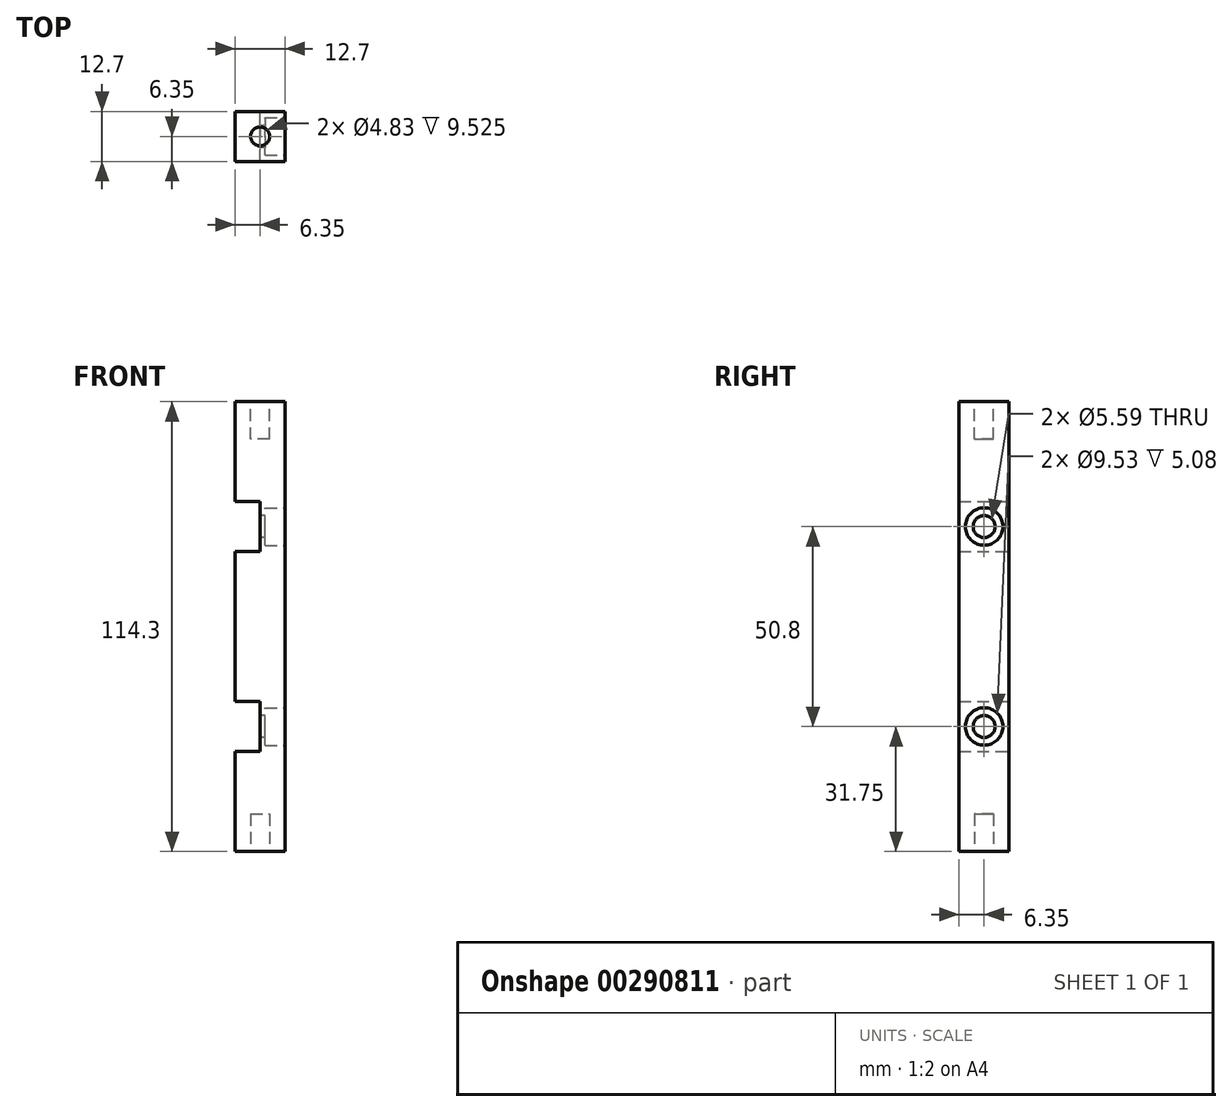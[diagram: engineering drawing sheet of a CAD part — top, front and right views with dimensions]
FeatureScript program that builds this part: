
annotation { "Feature Type Name" : "Feature", "Feature Type Description" : "" }
export const myFeature = defineFeature(function(context is Context, id is Id, definition is map)
    precondition{}
    {
        {
            var Q0;
            Q0=qCreatedBy(makeId("Right.planeOp"),FACE);
            var sketch = newSketch(context, id + "F0", { "sketchPlane" : qUnion([Q0])});
            skLineSegment(sketch, "E0.bottom", {"start": v(-12.7, 57.15) * mm, "end": v(0, 57.15) * mm});
            skLineSegment(sketch, "E0.top", {"start": v(-12.7, -57.15) * mm, "end": v(0, -57.15) * mm});
            skLineSegment(sketch, "E0.left", {"start": v(-12.7, 57.15) * mm, "end": v(-12.7, -57.15) * mm});
            skLineSegment(sketch, "E0.right", {"start": v(0, 57.15) * mm, "end": v(0, -57.15) * mm});
            skSolve(sketch);
        }
        {
            var Q0;
            Q0 = qSketchRegion(id + "F0", true);
            extrude(context, id + "F1", {"entities" : qUnion([Q0]), "depth" : 12.7 * mm});
        }
        {
            var Q0;
            Q0=makeQuery(id+"F1.opExtrude","SWEPT_FACE",FACE,{"disambiguationData":[OSD([sQuery(id+"F0.wireOp",EDGE,"E0.right")])]});
            var sketch = newSketch(context, id + "F2", { "sketchPlane" : qUnion([Q0])});
            skLineSegment(sketch, "E1.bottom", {"start": v(-6.35, 19.05) * mm, "end": v(0, 19.05) * mm});
            skLineSegment(sketch, "E1.top", {"start": v(-6.35, 31.75) * mm, "end": v(0, 31.75) * mm});
            skLineSegment(sketch, "E1.left", {"start": v(-6.35, 19.05) * mm, "end": v(-6.35, 31.75) * mm});
            skLineSegment(sketch, "E1.right", {"start": v(0, 19.05) * mm, "end": v(0, 31.75) * mm});
            skLineSegment(sketch, "E2.0.1.0", {"start": v(0, -31.75) * mm, "end": v(0, -19.05) * mm});
            skLineSegment(sketch, "E2.0.1.1", {"start": v(-6.35, -31.75) * mm, "end": v(0, -31.75) * mm});
            skLineSegment(sketch, "E2.0.1.2", {"start": v(-6.35, -19.05) * mm, "end": v(0, -19.05) * mm});
            skLineSegment(sketch, "E2.0.1.3", {"start": v(-6.35, -31.75) * mm, "end": v(-6.35, -19.05) * mm});
            skLineSegment(sketch, "E2.direction1", {"start": v(-6.35, 19.05) * mm, "end": v(-6.35, 19.05) * mm});
            skLineSegment(sketch, "E2.direction2", {"start": v(-6.35, 19.05) * mm, "end": v(-6.35, -31.75) * mm, "construction": true});
            skSolve(sketch);
        }
        {
            var Q0;
            Q0 = qSketchRegion(id + "F2", true);
            extrude(context, id + "F3", {"entities" : qUnion([Q0]), "operationType" : NewBodyOperationType.REMOVE, "endBound" : BoundingType.THROUGH_ALL, "oppositeDirection" : true, "depth" : 25.4 * mm});
        }
        {
            var Q0;
            Q0=makeQuery(id+"F3.boolean.opBoolean","COPY",FACE,{"derivedFrom":makeQuery(id+"F3.opExtrude","SWEPT_FACE",FACE,{"disambiguationData":[OSD([sQuery(id+"F2.wireOp",EDGE,"E1.left")])]})});
            var sketch = newSketch(context, id + "F4", { "sketchPlane" : qUnion([Q0])});
            skCircle(sketch, "E3", {"center": v(6.35, 25.4) * mm, "radius": 2.8 * mm});
            skCircle(sketch, "E4.0.1.0", {"center": v(6.35, -25.4) * mm, "radius": 2.8 * mm});
            skLineSegment(sketch, "E4.direction1", {"start": v(6.35, 25.4) * mm, "end": v(6.35, 25.4) * mm});
            skLineSegment(sketch, "E4.direction2", {"start": v(6.35, 25.4) * mm, "end": v(6.35, -25.4) * mm, "construction": true});
            skSolve(sketch);
        }
        {
            var Q0;
            Q0 = qSketchRegion(id + "F4", true);
            extrude(context, id + "F5", {"entities" : qUnion([Q0]), "operationType" : NewBodyOperationType.REMOVE, "endBound" : BoundingType.THROUGH_ALL, "oppositeDirection" : true, "depth" : 25.4 * mm});
        }
        {
            var Q0;
            Q0=makeQuery(id+"F1.opExtrude","CAP_FACE",FACE,{"disambiguationData":[OSD([sQuery(id+"F0.wireOp",EDGE,"E0.bottom"),sQuery(id+"F0.wireOp",EDGE,"E0.top"),sQuery(id+"F0.wireOp",EDGE,"E0.left"),sQuery(id+"F0.wireOp",EDGE,"E0.right")])],"isStart":false});
            var sketch = newSketch(context, id + "F6", { "sketchPlane" : qUnion([Q0])});
            skCircle(sketch, "E5", {"center": v(-6.35, 25.4) * mm, "radius": 4.76 * mm});
            skCircle(sketch, "E6.0.1.0", {"center": v(-6.35, -25.4) * mm, "radius": 4.76 * mm});
            skLineSegment(sketch, "E6.direction1", {"start": v(-6.35, 25.4) * mm, "end": v(-6.35, 25.4) * mm});
            skLineSegment(sketch, "E6.direction2", {"start": v(-6.35, 25.4) * mm, "end": v(-6.35, -25.4) * mm, "construction": true});
            skSolve(sketch);
        }
        {
            var Q0;
            Q0 = qSketchRegion(id + "F6", true);
            extrude(context, id + "F7", {"entities" : qUnion([Q0]), "operationType" : NewBodyOperationType.REMOVE, "oppositeDirection" : true, "depth" : 5.08 * mm});
        }
        {
            var Q0;
            Q0=makeQuery(id+"F1.opExtrude","SWEPT_FACE",FACE,{"disambiguationData":[OSD([sQuery(id+"F0.wireOp",EDGE,"E0.bottom")])]});
            var sketch = newSketch(context, id + "F8", { "sketchPlane" : qUnion([Q0])});
            skCircle(sketch, "E7", {"center": v(6.35, -6.35) * mm, "radius": 2.41 * mm});
            skSolve(sketch);
        }
        {
            var Q0;
            Q0 = qSketchRegion(id + "F8", true);
            extrude(context, id + "F9", {"entities" : qUnion([Q0]), "operationType" : NewBodyOperationType.REMOVE, "oppositeDirection" : true, "depth" : 9.52 * mm});
        }
        {
            var Q0;
            Q0=makeQuery(id+"F1.opExtrude","SWEPT_FACE",FACE,{"disambiguationData":[OSD([sQuery(id+"F0.wireOp",EDGE,"E0.top")])]});
            var sketch = newSketch(context, id + "F10", { "sketchPlane" : qUnion([Q0])});
            skCircle(sketch, "E8", {"center": v(6.35, 6.35) * mm, "radius": 2.41 * mm});
            skSolve(sketch);
        }
        {
            var Q0;
            Q0 = qSketchRegion(id + "F10", true);
            extrude(context, id + "F11", {"entities" : qUnion([Q0]), "operationType" : NewBodyOperationType.REMOVE, "oppositeDirection" : true, "depth" : 9.52 * mm});
        }
    });
